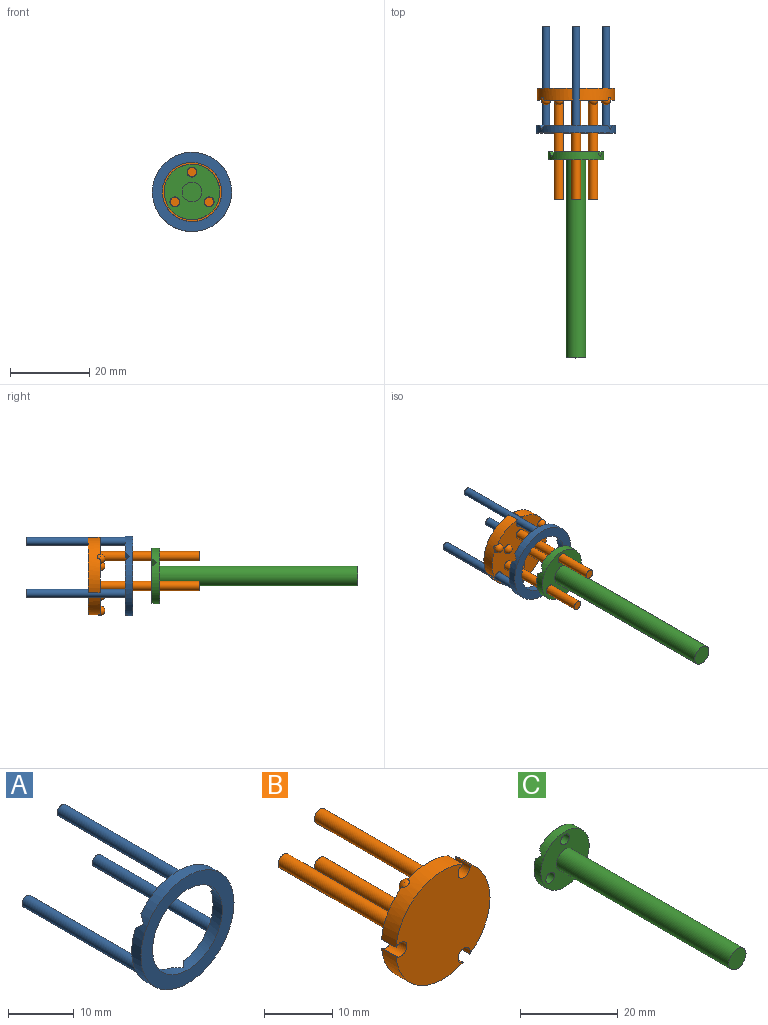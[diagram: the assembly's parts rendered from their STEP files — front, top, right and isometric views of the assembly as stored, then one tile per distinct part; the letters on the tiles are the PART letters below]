
ASSEMBLY  parts=3 mates=4
PART A: 18 faces, bbox 20x27x20 mm
  f0: cylinder r=7.5mm len=15mm, axis (0,1,0), area 89.9mm2, adj f2,f3,f4,f5,f6,f7,f8,f9
  f1: cylinder r=10mm len=20mm, axis (0,1,0), area 121.3mm2, adj f2,f3,f4,f5,f6,f7,f8,f9
  f2: plane 13.85x8.8mm, normal (0,1,0), area 36.7mm2, adj f0,f1,f6,f11,f14
  f3: plane 16x5.26mm, normal (0,1,0), area 36.7mm2, adj f0,f1,f9,f10,f12
  f4: plane 20x20mm, normal (0,-1,0), area 137.4mm2, adj f0,f1
  f5: plane 13.85x8.8mm, normal (0,1,0), area 36.7mm2, adj f0,f1,f7,f8,f16
  f6: plane 2.6x1.2mm, normal (-0.71,0.71,0), area 4.3mm2, adj f0,f1,f2,f7
  f7: plane 2.6x1.2mm, normal (0.71,0.71,0), area 4.3mm2, adj f0,f1,f5,f6
  f8: plane 2.71x2.34mm, normal (0.35,0.71,0.61), area 4.3mm2, adj f0,f1,f5,f9
  f9: plane 2.85x2.26mm, normal (-0.35,0.71,-0.61), area 4.3mm2, adj f0,f1,f3,f8
  f10: plane 2.85x2.26mm, normal (0.35,0.71,-0.61), area 4.3mm2, adj f0,f1,f3,f11
  f11: plane 2.71x2.34mm, normal (-0.35,0.71,0.61), area 4.3mm2, adj f0,f1,f2,f10
  f12: cylinder r=1mm len=25mm, axis (0,-1,0), area 157.1mm2, adj f3,f13
  f13: plane 2x2mm, normal (0,1,0), area 3.1mm2, adj f12
  f14: cylinder r=1mm len=25mm, axis (0,-1,0), area 157.1mm2, adj f2,f15
  f15: plane 2x2mm, normal (0,1,0), area 3.1mm2, adj f14
  f16: cylinder r=1mm len=25mm, axis (0,-1,0), area 157.1mm2, adj f5,f17
  f17: plane 2x2mm, normal (0,1,0), area 3.1mm2, adj f16
PART B: 20 faces, bbox 19.7x28x19.5 mm
  f0: cylinder r=9.75mm len=16.04mm, axis (0,1,0), area 55.8mm2, adj f2,f3,f5,f16,f19
  f1: cylinder r=9.75mm len=13.89mm, axis (0,1,0), area 55.8mm2, adj f2,f3,f6,f13,f19
  f2: plane 19.5x19.47mm, normal (0,-1,0), area 284.7mm2, adj f0,f1,f4,f13,f16,f19
  f3: plane 19.5x19.44mm, normal (0,1,0), area 245mm2, adj f0,f1,f4,f5,f6,f7,f8,f9
  f4: cylinder r=9.75mm len=13.89mm, axis (0,1,0), area 55.8mm2, adj f2,f3,f7,f13,f16
  f5: sphere r=1.2mm, area 9.8mm2, adj f0,f3
  f6: sphere r=1.2mm, area 9.8mm2, adj f1,f3
  f7: sphere r=1.2mm, area 9.8mm2, adj f3,f4
  f8: sphere r=1.2mm, area 9mm2, adj f3
  f9: sphere r=1.2mm, area 9mm2, adj f3
  f10: sphere r=1.2mm, area 9mm2, adj f3
  f11: cylinder r=1.18mm len=25mm, axis (0,-1,0), area 185.9mm2, adj f3,f12
  f12: plane 2.37x2.37mm, normal (0,1,0), area 4.4mm2, adj f11
  f13: cylinder r=1.25mm len=3mm, axis (0,1,0), area 18.4mm2, adj f1,f2,f3,f4
  f14: cylinder r=1.18mm len=25mm, axis (0,-1,0), area 185.9mm2, adj f3,f15
  f15: plane 2.37x2.37mm, normal (0,1,0), area 4.4mm2, adj f14
  f16: cylinder r=1.25mm len=3mm, axis (0,1,0), area 18.4mm2, adj f0,f2,f3,f4
  f17: cylinder r=1.18mm len=25mm, axis (0,-1,0), area 185.9mm2, adj f3,f18
  f18: plane 2.37x2.37mm, normal (0,1,0), area 4.4mm2, adj f17
  f19: cylinder r=1.25mm len=3mm, axis (0,1,0), area 18.4mm2, adj f0,f1,f2,f3
PART C: 18 faces, bbox 14x52x14 mm
  f0: cylinder r=7mm len=14mm, axis (0,1,0), area 83.6mm2, adj f1,f3,f4,f5,f6,f7,f8,f10
  f1: plane 9.31x5.8mm, normal (0,1,0), area 30.5mm2, adj f0,f3,f11,f12
  f2: cylinder r=1mm len=2mm, axis (0,1,0), area 8mm2, adj f3,f4,f6,f10,f12,f13,f17
  f3: plane 6.5x1.2mm, normal (-0.71,0.71,0), area 10.5mm2, adj f0,f1,f2,f6,f12
  f4: plane 6.07x3.99mm, normal (-0.35,0.71,-0.61), area 10.5mm2, adj f0,f2,f5,f10,f13
  f5: plane 10.75x5.61mm, normal (0,1,0), area 30.5mm2, adj f0,f4,f9,f13
  f6: plane 6.5x1.2mm, normal (0.71,0.71,0), area 10.5mm2, adj f0,f2,f3,f7,f10
  f7: plane 9.31x5.8mm, normal (0,1,0), area 30.5mm2, adj f0,f6,f10,f14
  f8: plane 14x14mm, normal (0,-1,0), area 119.6mm2, adj f0,f9,f11,f14,f16
  f9: cylinder r=1.25mm len=2.5mm, axis (0,1,0), area 15.7mm2, adj f5,f8
  f10: plane 5.71x4.2mm, normal (0.35,0.71,0.61), area 10.5mm2, adj f0,f2,f4,f6,f7
  f11: cylinder r=1.25mm len=2.5mm, axis (0,1,0), area 15.7mm2, adj f1,f8
  f12: plane 5.71x4.2mm, normal (-0.35,0.71,0.61), area 10.5mm2, adj f0,f1,f2,f3,f13
  f13: plane 6.07x3.99mm, normal (0.35,0.71,-0.61), area 10.5mm2, adj f0,f2,f4,f5,f12
  f14: cylinder r=1.25mm len=2.5mm, axis (0,1,0), area 15.7mm2, adj f7,f8
  f15: plane 5x5mm, normal (0,-1,0), area 19.6mm2, adj f16
  f16: cylinder r=2.5mm len=50mm, axis (0,1,0), area 785.4mm2, adj f8,f15
  f17: plane 2x2mm, normal (0,1,0), area 3.1mm2, adj f2
PLACE A at identity fixed
PLACE B rot(axis=(0.97,0,0.26),180deg) t=(0,6.3,0)mm
PLACE C rot(axis=(0,-1,0),120deg) t=(0,-6.79,0)mm
MATE cylindrical C.f14 <-> B.f14  axis (0,1,0) through (4.33,-6.79,-2.5)mm
MATE cylindrical B.f19 <-> A.f12  axis (0,-1,0) through (0,6.3,8.75)mm
MATE cylindrical C.f11 <-> B.f17  axis (0,1,0) through (0,-6.79,5)mm
MATE cylindrical B.f16 <-> A.f14  axis (0,1,0) through (7.58,9.3,-4.37)mm
